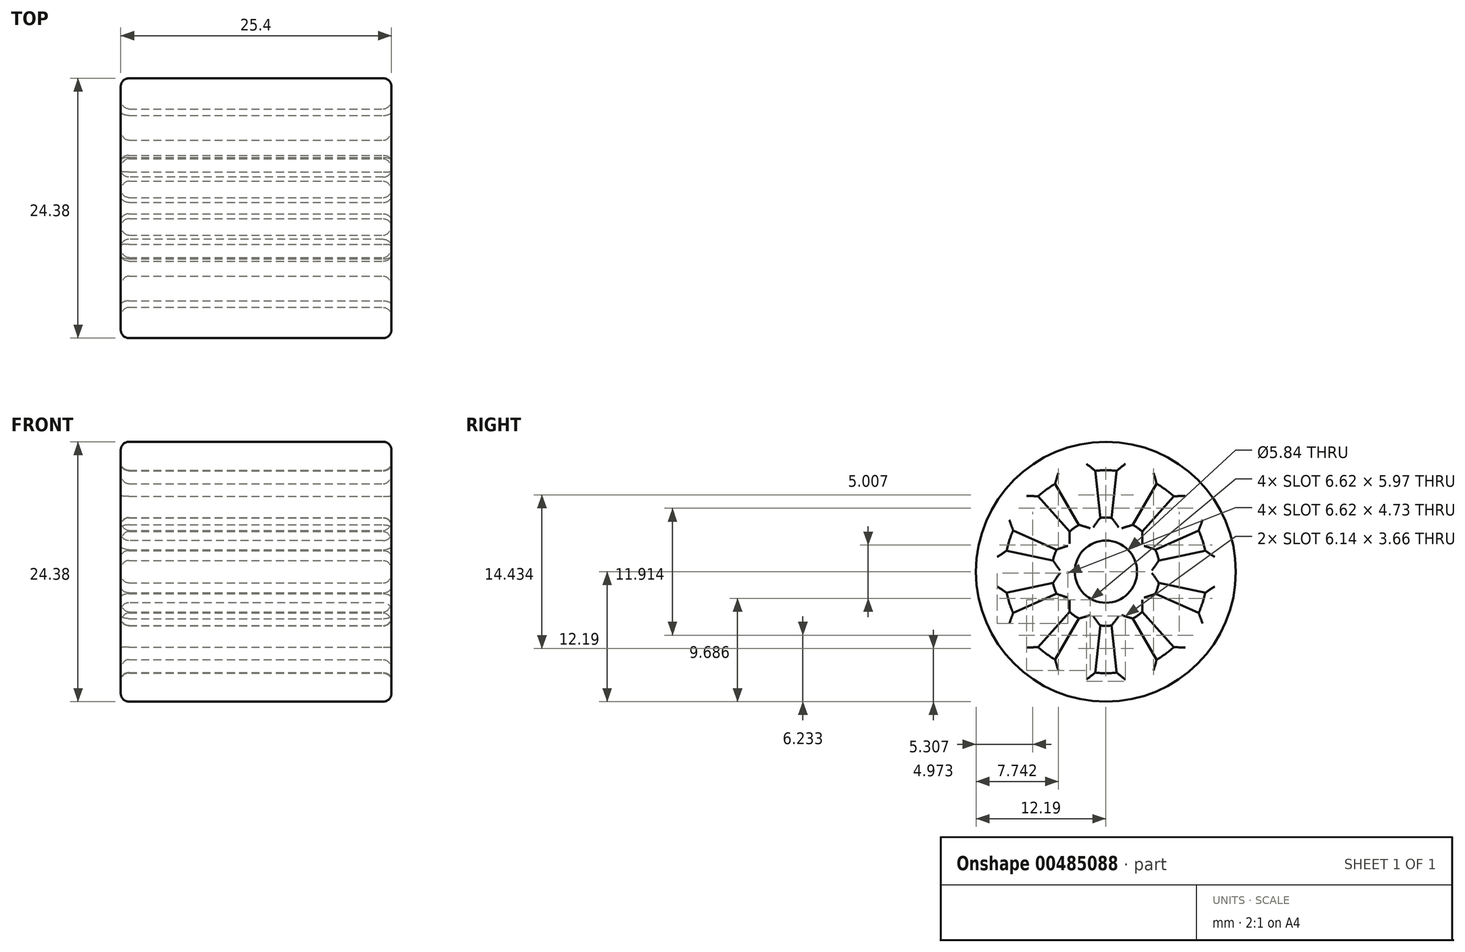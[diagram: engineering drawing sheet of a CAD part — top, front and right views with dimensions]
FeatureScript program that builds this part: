
annotation { "Feature Type Name" : "Feature", "Feature Type Description" : "" }
export const myFeature = defineFeature(function(context is Context, id is Id, definition is map)
    precondition{}
    {
        {
            var Q0;
            Q0=qCreatedBy(makeId("Right.planeOp"),FACE);
            var sketch = newSketch(context, id + "F0", { "sketchPlane" : qUnion([Q0])});
            skCircle(sketch, "E0", {"center": v(0, 0) * mm, "radius": 12.2 * mm});
            skCircle(sketch, "E1", {"center": v(0, 0) * mm, "radius": 2.92 * mm});
            skSolve(sketch);
        }
        {
            var Q0;
            Q0 = qSketchRegion(id + "F0", true);
            extrude(context, id + "F1", {"entities" : qUnion([Q0]), "depth" : 25.4 * mm});
        }
        {
            var Q0;
            Q0=makeQuery(id+"F1.opExtrude","CAP_FACE",FACE,{"disambiguationData":[OSD([sQuery(id+"F0.wireOp",EDGE,"E0"),sQuery(id+"F0.wireOp",EDGE,"E1")])],"isStart":false});
            var sketch = newSketch(context, id + "F2", { "sketchPlane" : qUnion([Q0])});
            skArc(sketch, "E2", {"start": v(0.53, 5.05) * mm, "mid": v(0, 5.08) * mm, "end": v(-0.53, 5.05) * mm});
            skArc(sketch, "E3", {"start": v(1, 9.47) * mm, "mid": v(0, 9.53) * mm, "end": v(-1, 9.47) * mm});
            skLineSegment(sketch, "E4", {"start": v(0.53, 5.05) * mm, "end": v(1, 9.47) * mm});
            skLineSegment(sketch, "E5.MirrorCS", {"start": v(-0.53, 5.05) * mm, "end": v(-1, 9.47) * mm});
            skArc(sketch, "E6.1.1", {"start": v(-2.54, 4.4) * mm, "mid": v(-2.99, 4.1) * mm, "end": v(-3.4, 3.78) * mm});
            skLineSegment(sketch, "E6.1.2", {"start": v(-2.54, 4.4) * mm, "end": v(-4.76, 8.25) * mm});
            skArc(sketch, "E6.1.3", {"start": v(-4.76, 8.25) * mm, "mid": v(-5.6, 7.7) * mm, "end": v(-6.37, 7.08) * mm});
            skLineSegment(sketch, "E6.1.4", {"start": v(-3.4, 3.78) * mm, "end": v(-6.37, 7.08) * mm});
            skArc(sketch, "E6.2.1", {"start": v(-4.64, 2.07) * mm, "mid": v(-4.83, 1.57) * mm, "end": v(-4.97, 1.06) * mm});
            skLineSegment(sketch, "E6.2.2", {"start": v(-4.64, 2.07) * mm, "end": v(-8.7, 3.87) * mm});
            skArc(sketch, "E6.2.3", {"start": v(-8.7, 3.87) * mm, "mid": v(-9.06, 2.94) * mm, "end": v(-9.32, 1.98) * mm});
            skLineSegment(sketch, "E6.2.4", {"start": v(-4.97, 1.06) * mm, "end": v(-9.32, 1.98) * mm});
            skArc(sketch, "E6.3.1", {"start": v(-4.97, -1.06) * mm, "mid": v(-4.83, -1.57) * mm, "end": v(-4.64, -2.07) * mm});
            skLineSegment(sketch, "E6.3.2", {"start": v(-4.97, -1.06) * mm, "end": v(-9.32, -1.98) * mm});
            skArc(sketch, "E6.3.3", {"start": v(-9.32, -1.98) * mm, "mid": v(-9.06, -2.94) * mm, "end": v(-8.7, -3.87) * mm});
            skLineSegment(sketch, "E6.3.4", {"start": v(-4.64, -2.07) * mm, "end": v(-8.7, -3.87) * mm});
            skArc(sketch, "E6.4.1", {"start": v(-3.4, -3.78) * mm, "mid": v(-2.99, -4.1) * mm, "end": v(-2.54, -4.4) * mm});
            skLineSegment(sketch, "E6.4.2", {"start": v(-3.4, -3.78) * mm, "end": v(-6.37, -7.08) * mm});
            skArc(sketch, "E6.4.3", {"start": v(-6.37, -7.08) * mm, "mid": v(-5.6, -7.7) * mm, "end": v(-4.76, -8.25) * mm});
            skLineSegment(sketch, "E6.4.4", {"start": v(-2.54, -4.4) * mm, "end": v(-4.76, -8.25) * mm});
            skArc(sketch, "E6.5.1", {"start": v(-0.53, -5.05) * mm, "mid": v(0, -5.08) * mm, "end": v(0.53, -5.05) * mm});
            skLineSegment(sketch, "E6.5.2", {"start": v(-0.53, -5.05) * mm, "end": v(-1, -9.47) * mm});
            skArc(sketch, "E6.5.3", {"start": v(-1, -9.47) * mm, "mid": v(0, -9.53) * mm, "end": v(1, -9.47) * mm});
            skLineSegment(sketch, "E6.5.4", {"start": v(0.53, -5.05) * mm, "end": v(1, -9.47) * mm});
            skArc(sketch, "E6.6.1", {"start": v(2.54, -4.4) * mm, "mid": v(2.99, -4.1) * mm, "end": v(3.4, -3.78) * mm});
            skLineSegment(sketch, "E6.6.2", {"start": v(2.54, -4.4) * mm, "end": v(4.76, -8.25) * mm});
            skArc(sketch, "E6.6.3", {"start": v(4.76, -8.25) * mm, "mid": v(5.6, -7.7) * mm, "end": v(6.37, -7.08) * mm});
            skLineSegment(sketch, "E6.6.4", {"start": v(3.4, -3.78) * mm, "end": v(6.37, -7.08) * mm});
            skArc(sketch, "E6.7.1", {"start": v(4.64, -2.07) * mm, "mid": v(4.83, -1.57) * mm, "end": v(4.97, -1.06) * mm});
            skLineSegment(sketch, "E6.7.2", {"start": v(4.64, -2.07) * mm, "end": v(8.7, -3.87) * mm});
            skArc(sketch, "E6.7.3", {"start": v(8.7, -3.87) * mm, "mid": v(9.06, -2.94) * mm, "end": v(9.32, -1.98) * mm});
            skLineSegment(sketch, "E6.7.4", {"start": v(4.97, -1.06) * mm, "end": v(9.32, -1.98) * mm});
            skArc(sketch, "E7.1.8.0", {"start": v(4.97, 1.06) * mm, "mid": v(4.83, 1.57) * mm, "end": v(4.64, 2.07) * mm});
            skLineSegment(sketch, "E7.5.8.0", {"start": v(4.97, 1.06) * mm, "end": v(9.32, 1.98) * mm});
            skArc(sketch, "E7.8.8.0", {"start": v(9.32, 1.98) * mm, "mid": v(9.06, 2.94) * mm, "end": v(8.7, 3.87) * mm});
            skLineSegment(sketch, "E7.12.8.0", {"start": v(4.64, 2.07) * mm, "end": v(8.7, 3.87) * mm});
            skArc(sketch, "E7.1.9.0", {"start": v(3.4, 3.78) * mm, "mid": v(2.99, 4.1) * mm, "end": v(2.54, 4.4) * mm});
            skLineSegment(sketch, "E7.5.9.0", {"start": v(3.4, 3.78) * mm, "end": v(6.37, 7.08) * mm});
            skArc(sketch, "E7.8.9.0", {"start": v(6.37, 7.08) * mm, "mid": v(5.6, 7.7) * mm, "end": v(4.76, 8.25) * mm});
            skLineSegment(sketch, "E7.12.9.0", {"start": v(2.54, 4.4) * mm, "end": v(4.76, 8.25) * mm});
            skSolve(sketch);
        }
        {
            var Q0;
            Q0 = qSketchRegion(id + "F2", true);
            extrude(context, id + "F3", {"entities" : qUnion([Q0]), "operationType" : NewBodyOperationType.REMOVE, "endBound" : BoundingType.THROUGH_ALL, "oppositeDirection" : true, "depth" : 25.4 * mm});
        }
        {
            var Q0;
            Q0=makeQuery(id+"F1.opExtrude","CAP_FACE",FACE,{"disambiguationData":[OSD([sQuery(id+"F0.wireOp",EDGE,"E0"),sQuery(id+"F0.wireOp",EDGE,"E1")])],"isStart":false});
            var Q1;
            Q1=makeQuery(id+"F1.opExtrude","CAP_FACE",FACE,{"disambiguationData":[OSD([sQuery(id+"F0.wireOp",EDGE,"E0"),sQuery(id+"F0.wireOp",EDGE,"E1")])],"isStart":true});
            fillet(context, id + "F4", {"entities" : qUnion([Q0, Q1]), "radius" : 0.76 * mm, "tangentPropagation" : true, "allowEdgeOverflow" : false});
        }
    });
